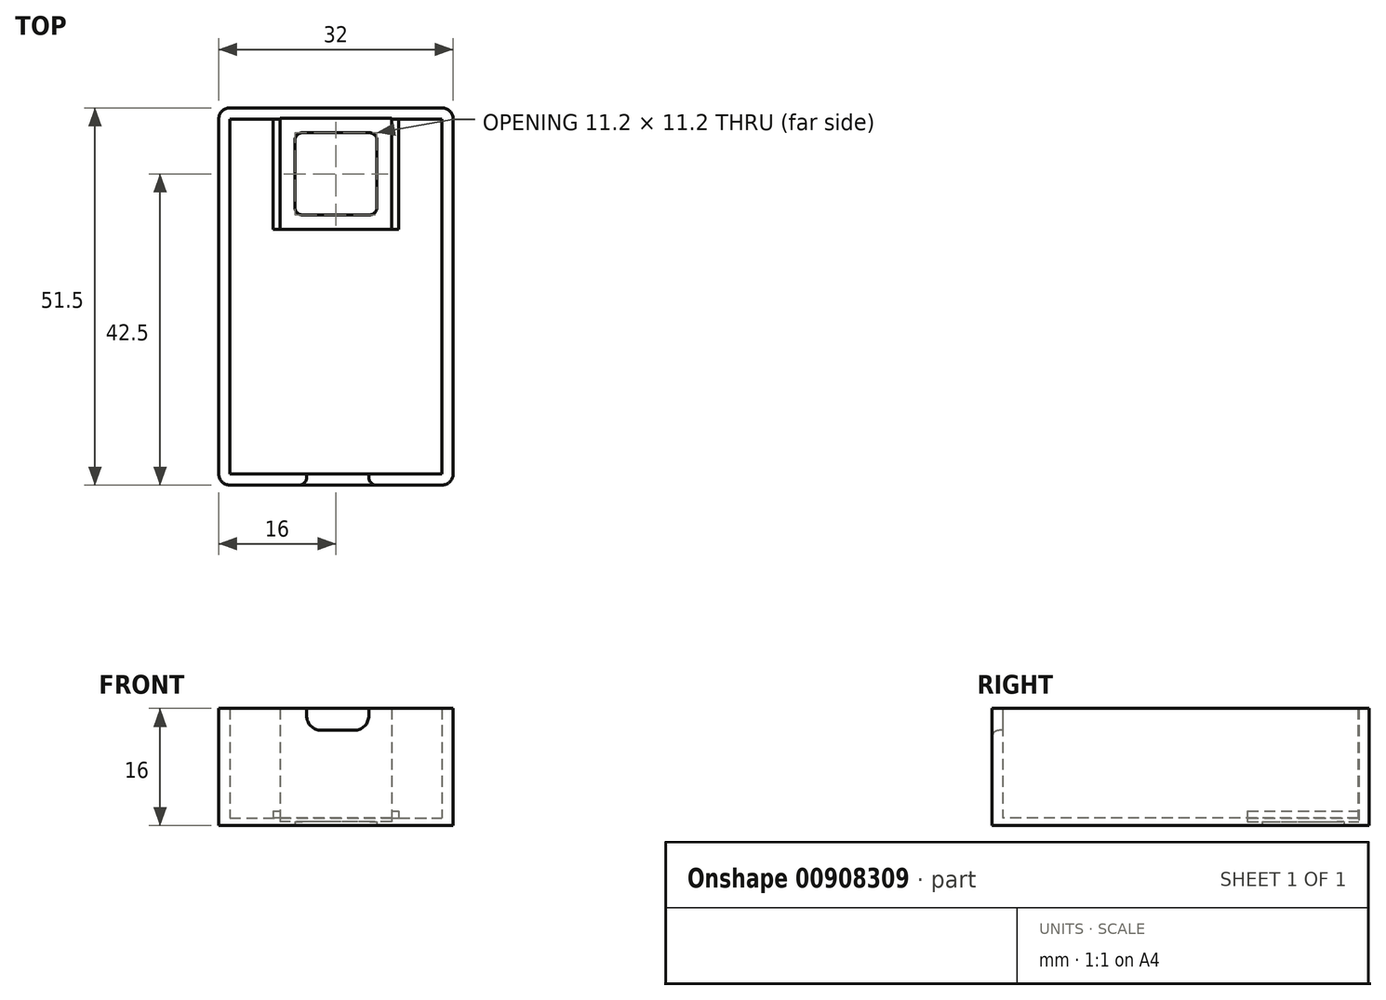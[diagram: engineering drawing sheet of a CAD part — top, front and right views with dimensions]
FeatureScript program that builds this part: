
annotation { "Feature Type Name" : "Feature", "Feature Type Description" : "" }
export const myFeature = defineFeature(function(context is Context, id is Id, definition is map)
    precondition{}
    {
        {
            var Q0;
            Q0=qCreatedBy(makeId("Top.planeOp"),FACE);
            var sketch = newSketch(context, id + "F0", { "sketchPlane" : qUnion([Q0])});
            skLineSegment(sketch, "E0.bottom", {"start": v(13, -22.75) * mm, "end": v(-13, -22.75) * mm});
            skLineSegment(sketch, "E0.top", {"start": v(13, 22.75) * mm, "end": v(-13, 22.75) * mm});
            skLineSegment(sketch, "E0.left", {"start": v(13, -22.75) * mm, "end": v(13, 22.75) * mm});
            skLineSegment(sketch, "E0.right", {"start": v(-13, -22.75) * mm, "end": v(-13, 22.75) * mm});
            skPoint(sketch, "E0.middle", {"position": v(0, 0) * mm});
            skLineSegment(sketch, "E1.0", {"start": v(14.5, -24.25) * mm, "end": v(14.5, 24.25) * mm});
            skLineSegment(sketch, "E1.1", {"start": v(14.5, -24.25) * mm, "end": v(-14.5, -24.25) * mm});
            skLineSegment(sketch, "E1.2", {"start": v(-14.5, -24.25) * mm, "end": v(-14.5, 24.25) * mm});
            skLineSegment(sketch, "E1.3", {"start": v(14.5, 24.25) * mm, "end": v(-14.5, 24.25) * mm});
            skLineSegment(sketch, "E2.0", {"start": v(16, -25.75) * mm, "end": v(16, 25.75) * mm});
            skLineSegment(sketch, "E2.1", {"start": v(16, -25.75) * mm, "end": v(-16, -25.75) * mm});
            skLineSegment(sketch, "E2.2", {"start": v(-16, -25.75) * mm, "end": v(-16, 25.75) * mm});
            skLineSegment(sketch, "E2.3", {"start": v(16, 25.75) * mm, "end": v(-16, 25.75) * mm});
            skLineSegment(sketch, "E3", {"start": v(-13, 22.75) * mm, "end": v(-13, 16.75) * mm, "construction": true});
            skLineSegment(sketch, "E4", {"start": v(-13, 16.75) * mm, "end": v(0, 16.75) * mm, "construction": true});
            skLineSegment(sketch, "E5.bottom", {"start": v(7.6, 9.15) * mm, "end": v(-7.6, 9.15) * mm});
            skLineSegment(sketch, "E5.top", {"start": v(7.6, 24.35) * mm, "end": v(-7.6, 24.35) * mm});
            skLineSegment(sketch, "E5.left", {"start": v(7.6, 9.15) * mm, "end": v(7.6, 24.35) * mm});
            skLineSegment(sketch, "E5.right", {"start": v(-7.6, 9.15) * mm, "end": v(-7.6, 24.35) * mm});
            skPoint(sketch, "E5.middle", {"position": v(0, 16.75) * mm});
            skLineSegment(sketch, "E6.0", {"start": v(-5.6, 11.15) * mm, "end": v(-5.6, 22.35) * mm});
            skLineSegment(sketch, "E6.1", {"start": v(5.6, 11.15) * mm, "end": v(-5.6, 11.15) * mm});
            skLineSegment(sketch, "E6.2", {"start": v(5.6, 11.15) * mm, "end": v(5.6, 22.35) * mm});
            skLineSegment(sketch, "E6.3", {"start": v(5.6, 22.35) * mm, "end": v(-5.6, 22.35) * mm});
            skSolve(sketch);
        }
        {
            var Q0;
            Q0 = qSketchRegion(id + "F0", true);
            var Q1;
            Q1=makeQuery(id+"F0.imprint","IMPRINT",FACE,{"disambiguationData":[TD([[makeQuery(id+"F0.imprint","IMPRINT",EDGE,{"derivedFrom":sQuery(id+"F0.wireOp",EDGE,"E0.bottom")}),1.0]])]});
            var Q2;
            Q2=makeQuery(id+"F0.imprint","IMPRINT",FACE,{"disambiguationData":[TD([[makeQuery(id+"F0.imprint","IMPRINT",EDGE,{"derivedFrom":sQuery(id+"F0.wireOp",EDGE,"E0.bottom")}),-1.0]])]});
            extrude(context, id + "F1", {"entities" : qUnion([Q0, Q1, Q2]), "depth" : 1 * mm, "offsetDistance" : 25 * mm});
        }
        {
            var Q0;
            Q0 = qSketchRegion(id + "F0", true);
            extrude(context, id + "F2", {"entities" : qUnion([Q0]), "operationType" : NewBodyOperationType.ADD, "depth" : 16 * mm, "offsetDistance" : 25 * mm});
        }
        {
            var Q0;
            {var subQ0=sQuery(id+"F0.wireOp",EDGE,"E2.2");var subQ1=sQuery(id+"F0.wireOp",EDGE,"E2.1");Q0=makeQuery(id+"F2.boolean.opBoolean","MERGE",EDGE,{"derivedFrom":[makeQuery(id+"F1.opExtrude","SWEPT_EDGE",EDGE,{"disambiguationData":[OSD([subQ1,subQ0])]}),makeQuery(id+"F2.opExtrude","SWEPT_EDGE",EDGE,{"disambiguationData":[OSD([subQ1,subQ0])]})]});}
            var Q1;
            {var subQ0=sQuery(id+"F0.wireOp",EDGE,"E2.1");var subQ1=sQuery(id+"F0.wireOp",EDGE,"E2.0");Q1=makeQuery(id+"F2.boolean.opBoolean","MERGE",EDGE,{"derivedFrom":[makeQuery(id+"F1.opExtrude","SWEPT_EDGE",EDGE,{"disambiguationData":[OSD([subQ1,subQ0])]}),makeQuery(id+"F2.opExtrude","SWEPT_EDGE",EDGE,{"disambiguationData":[OSD([subQ1,subQ0])]})]});}
            var Q2;
            {var subQ0=sQuery(id+"F0.wireOp",EDGE,"E2.3");var subQ1=sQuery(id+"F0.wireOp",EDGE,"E2.2");Q2=makeQuery(id+"F2.boolean.opBoolean","MERGE",EDGE,{"derivedFrom":[makeQuery(id+"F1.opExtrude","SWEPT_EDGE",EDGE,{"disambiguationData":[OSD([subQ1,subQ0])]}),makeQuery(id+"F2.opExtrude","SWEPT_EDGE",EDGE,{"disambiguationData":[OSD([subQ1,subQ0])]})]});}
            var Q3;
            {var subQ0=sQuery(id+"F0.wireOp",EDGE,"E2.3");var subQ1=sQuery(id+"F0.wireOp",EDGE,"E2.0");Q3=makeQuery(id+"F2.boolean.opBoolean","MERGE",EDGE,{"derivedFrom":[makeQuery(id+"F1.opExtrude","SWEPT_EDGE",EDGE,{"disambiguationData":[OSD([subQ1,subQ0])]}),makeQuery(id+"F2.opExtrude","SWEPT_EDGE",EDGE,{"disambiguationData":[OSD([subQ1,subQ0])]})]});}
            fillet(context, id + "F3", {"entities" : qUnion([Q0, Q1, Q2, Q3]), "radius" : 1.5 * mm, "tangentPropagation" : true, "allowEdgeOverflow" : false});
        }
        {
            var Q0;
            {var subQ0=sQuery(id+"F0.wireOp",EDGE,"E2.1");Q0=makeQuery(id+"F2.boolean.opBoolean","MERGE",FACE,{"derivedFrom":[makeQuery(id+"F1.opExtrude","SWEPT_FACE",FACE,{"disambiguationData":[OSD([subQ0])]}),makeQuery(id+"F2.opExtrude","SWEPT_FACE",FACE,{"disambiguationData":[OSD([subQ0])]})]});}
            var sketch = newSketch(context, id + "F4", { "sketchPlane" : qUnion([Q0])});
            skLineSegment(sketch, "E7.bottom", {"start": v(-4, 16) * mm, "end": v(4.5, 16) * mm});
            skLineSegment(sketch, "E7.top", {"start": v(-4, 13) * mm, "end": v(4.5, 13) * mm});
            skLineSegment(sketch, "E7.left", {"start": v(-4, 16) * mm, "end": v(-4, 13) * mm});
            skLineSegment(sketch, "E7.right", {"start": v(4.5, 16) * mm, "end": v(4.5, 13) * mm});
            skLineSegment(sketch, "E8", {"start": v(-4, 16) * mm, "end": v(-14.5, 16) * mm});
            skSolve(sketch);
        }
        {
            var Q0;
            Q0=makeQuery(id+"F4.imprint","IMPRINT",FACE,{"disambiguationData":[TD([[makeQuery(id+"F4.imprint","IMPRINT",EDGE,{"derivedFrom":sQuery(id+"F4.wireOp",EDGE,"E7.bottom")}),1.0]])]});
            extrude(context, id + "F5", {"entities" : qUnion([Q0]), "operationType" : NewBodyOperationType.REMOVE, "oppositeDirection" : true, "depth" : 5 * mm, "offsetDistance" : 25 * mm});
        }
        {
            var Q0;
            Q0=makeQuery(id+"F5.boolean.opBoolean","COPY",EDGE,{"derivedFrom":makeQuery(id+"F5.opExtrude","SWEPT_EDGE",EDGE,{"disambiguationData":[OSD([sQuery(id+"F4.wireOp",EDGE,"E7.top"),sQuery(id+"F4.wireOp",EDGE,"E7.left")])]})});
            var Q1;
            Q1=makeQuery(id+"F5.boolean.opBoolean","COPY",EDGE,{"derivedFrom":makeQuery(id+"F5.opExtrude","SWEPT_EDGE",EDGE,{"disambiguationData":[OSD([sQuery(id+"F4.wireOp",EDGE,"E7.top"),sQuery(id+"F4.wireOp",EDGE,"E7.right")])]})});
            fillet(context, id + "F6", {"entities" : qUnion([Q0, Q1]), "radius" : 2 * mm, "tangentPropagation" : true, "allowEdgeOverflow" : false});
        }
        {
            var Q0;
            {var subQ0=sQuery(id+"F0.wireOp",EDGE,"E2.1");Q0=makeQuery(id+"F6.opFillet","BLEND_EDGE",EDGE,{"blendedFrom":[makeQuery(id+"F5.boolean.opBoolean","COPY",EDGE,{"derivedFrom":makeQuery(id+"F5.opExtrude","SWEPT_EDGE",EDGE,{"disambiguationData":[OSD([sQuery(id+"F4.wireOp",EDGE,"E7.top"),sQuery(id+"F4.wireOp",EDGE,"E7.left")])]})}),makeQuery(id+"F2.boolean.opBoolean","MERGE",FACE,{"derivedFrom":[makeQuery(id+"F1.opExtrude","SWEPT_FACE",FACE,{"disambiguationData":[OSD([subQ0])]}),makeQuery(id+"F2.opExtrude","SWEPT_FACE",FACE,{"disambiguationData":[OSD([subQ0])]})]})],"blendedInto":[makeQuery(id+"F2.boolean.opBoolean","MERGE",FACE,{"derivedFrom":[makeQuery(id+"F1.opExtrude","SWEPT_FACE",FACE,{"disambiguationData":[OSD([subQ0])]}),makeQuery(id+"F2.opExtrude","SWEPT_FACE",FACE,{"disambiguationData":[OSD([subQ0])]})]})]});}
            var Q1;
            Q1=makeQuery(id+"F5.boolean.opBoolean","COPY",EDGE,{"derivedFrom":makeQuery(id+"F5.opExtrude","CAP_EDGE",EDGE,{"disambiguationData":[OSD([sQuery(id+"F4.wireOp",EDGE,"E7.bottom")])],"isStart":true})});
            fillet(context, id + "F7", {"entities" : qUnion([Q0, Q1]), "radius" : 1 * mm, "tangentPropagation" : true, "allowEdgeOverflow" : false});
        }
        {
            var Q0;
            Q0=makeQuery(id+"F0.imprint","IMPRINT",FACE,{"disambiguationData":[TD([[makeQuery(id+"F0.imprint","IMPRINT",EDGE,{"derivedFrom":sQuery(id+"F0.wireOp",EDGE,"E5.bottom")}),-1.0]])]});
            var Q1;
            {var subQ5=sQuery(id+"F0.wireOp",EDGE,"E5.top");Q1=makeQuery(id+"F0.imprint","IMPRINT",FACE,{"disambiguationData":[TD([[makeQuery(id+"F0.imprint","IMPRINT",EDGE,{"derivedFrom":subQ5}),1.0]])]});}
            var Q2;
            {var subQ0=sQuery(id+"F0.wireOp",EDGE,"E5.left");var subQ1=sQuery(id+"F0.wireOp",EDGE,"E0.top");var subQ2=makeQuery(id+"F0.imprint","INTERSECT",VERTEX,{"derivedFrom":[subQ1,subQ0]});Q2=makeQuery(id+"F0.imprint","IMPRINT",FACE,{"disambiguationData":[TD([[makeQuery(id+"F0.imprint","IMPRINT",EDGE,{"disambiguationData":[TD([[subQ2,-1.0]])],"derivedFrom":subQ1}),-1.0]])]});}
            extrude(context, id + "F8", {"entities" : qUnion([Q0, Q1, Q2]), "operationType" : NewBodyOperationType.ADD, "depth" : 0.5 * mm, "offsetDistance" : 25 * mm});
        }
        {
            var Q0;
            Q0=makeQuery(id+"F8.opExtrude","SWEPT_EDGE",EDGE,{"disambiguationData":[OSD([sQuery(id+"F0.wireOp",EDGE,"E6.1"),sQuery(id+"F0.wireOp",EDGE,"E6.2")])]});
            var Q1;
            Q1=makeQuery(id+"F8.opExtrude","SWEPT_EDGE",EDGE,{"disambiguationData":[OSD([sQuery(id+"F0.wireOp",EDGE,"E6.0"),sQuery(id+"F0.wireOp",EDGE,"E6.1")])]});
            var Q2;
            Q2=makeQuery(id+"F8.opExtrude","SWEPT_EDGE",EDGE,{"disambiguationData":[OSD([sQuery(id+"F0.wireOp",EDGE,"E6.2"),sQuery(id+"F0.wireOp",EDGE,"E6.3")])]});
            var Q3;
            Q3=makeQuery(id+"F8.opExtrude","SWEPT_EDGE",EDGE,{"disambiguationData":[OSD([sQuery(id+"F0.wireOp",EDGE,"E6.0"),sQuery(id+"F0.wireOp",EDGE,"E6.3")])]});
            fillet(context, id + "F9", {"entities" : qUnion([Q0, Q1, Q2, Q3]), "radius" : 1 * mm, "tangentPropagation" : true, "allowEdgeOverflow" : false});
        }
        {
            var Q0;
            Q0=makeQuery(id+"F1.opExtrude","CAP_FACE",FACE,{"disambiguationData":[OSD([sQuery(id+"F0.wireOp",EDGE,"E2.0"),sQuery(id+"F0.wireOp",EDGE,"E2.1"),sQuery(id+"F0.wireOp",EDGE,"E2.2"),sQuery(id+"F0.wireOp",EDGE,"E2.3"),sQuery(id+"F0.wireOp",EDGE,"E5.bottom"),sQuery(id+"F0.wireOp",EDGE,"E5.top"),sQuery(id+"F0.wireOp",EDGE,"E5.left"),sQuery(id+"F0.wireOp",EDGE,"E5.right")])],"isStart":false});
            var sketch = newSketch(context, id + "F10", { "sketchPlane" : qUnion([Q0])});
            skLineSegment(sketch, "E9", {"start": v(-7.6, 9.15) * mm, "end": v(-8.6, 9.15) * mm});
            skLineSegment(sketch, "E10", {"start": v(-8.6, 9.15) * mm, "end": v(-8.6, 24.25) * mm});
            skLineSegment(sketch, "E11", {"start": v(-8.6, 24.25) * mm, "end": v(-7.6, 24.25) * mm});
            skLineSegment(sketch, "E12.0", {"start": v(-7.6, 9.15) * mm, "end": v(-7.6, 24.35) * mm});
            skLineSegment(sketch, "E13.0", {"start": v(7.6, 9.15) * mm, "end": v(7.6, 24.35) * mm});
            skLineSegment(sketch, "E14", {"start": v(7.6, 9.15) * mm, "end": v(8.6, 9.15) * mm});
            skLineSegment(sketch, "E15", {"start": v(8.6, 9.15) * mm, "end": v(8.6, 24.25) * mm});
            skLineSegment(sketch, "E16", {"start": v(8.6, 24.25) * mm, "end": v(7.6, 24.25) * mm});
            skSolve(sketch);
        }
        {
            var Q0;
            {var subQ0=sQuery(id+"F10.wireOp",EDGE,"E9");Q0=makeQuery(id+"F10.imprint","IMPRINT",FACE,{"disambiguationData":[TD([[makeQuery(id+"F10.imprint","IMPRINT",EDGE,{"derivedFrom":subQ0}),-1.0]])]});}
            var Q1;
            {var subQ0=sQuery(id+"F10.wireOp",EDGE,"E14");Q1=makeQuery(id+"F10.imprint","IMPRINT",FACE,{"disambiguationData":[TD([[makeQuery(id+"F10.imprint","IMPRINT",EDGE,{"derivedFrom":subQ0}),1.0]])]});}
            extrude(context, id + "F11", {"entities" : qUnion([Q0, Q1]), "operationType" : NewBodyOperationType.ADD, "depth" : 1 * mm, "offsetDistance" : 25 * mm});
        }
    });
